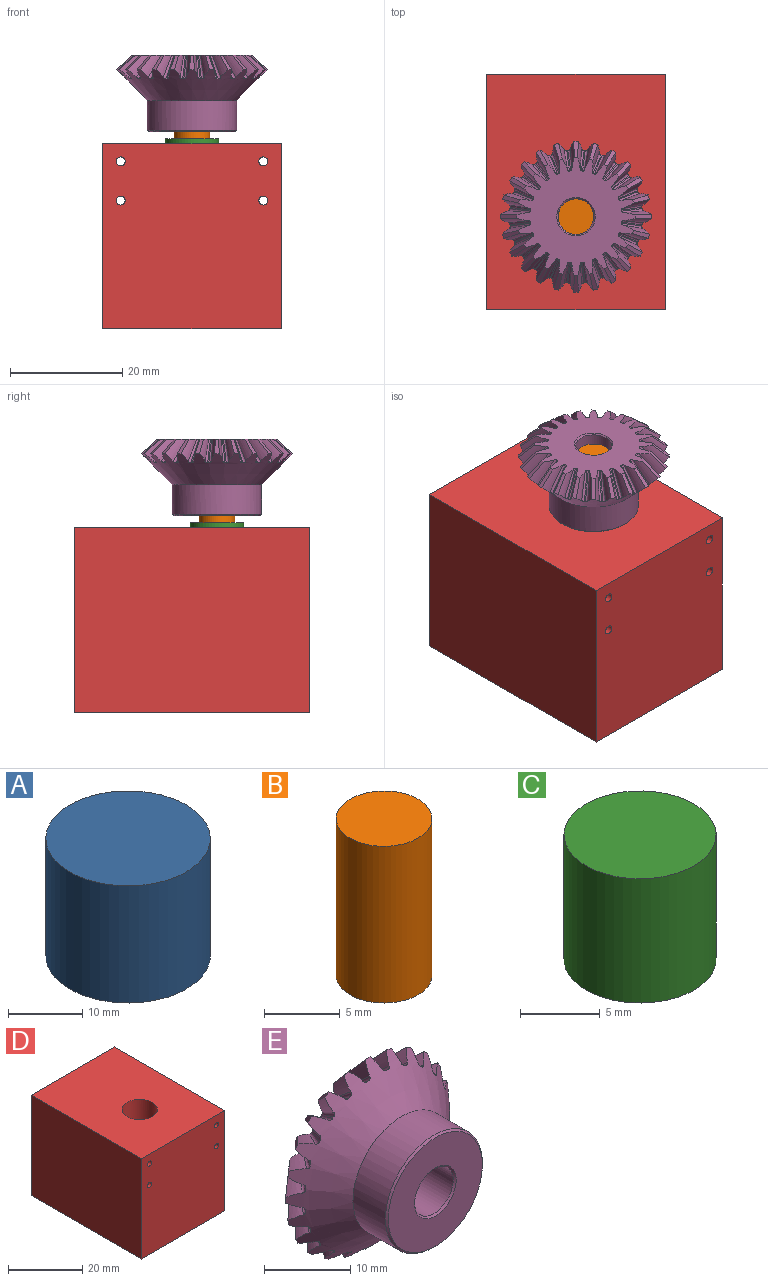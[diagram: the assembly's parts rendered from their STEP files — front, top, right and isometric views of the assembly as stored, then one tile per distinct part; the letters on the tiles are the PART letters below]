
ASSEMBLY  parts=5 mates=4
PART A: 3 faces, bbox 22.2x22.2x19.4 mm
  f0: cylinder r=11.11mm len=22.23mm, axis (0,0,-1), area 1353.2mm2, adj f1,f2
  f1: plane 22.23x22.23mm, normal (0,0,1), area 387.9mm2, adj f0
  f2: plane 22.23x22.23mm, normal (0,0,-1), area 387.9mm2, adj f0
PART B: 3 faces, bbox 6.4x6.4x12.7 mm
  f0: cylinder r=3.17mm len=12.7mm, axis (0,0,-1), area 253.4mm2, adj f1,f2
  f1: plane 6.35x6.35mm, normal (0,0,1), area 31.7mm2, adj f0
  f2: plane 6.35x6.35mm, normal (0,0,-1), area 31.7mm2, adj f0
PART C: 3 faces, bbox 9.5x9.5x9.5 mm
  f0: cylinder r=4.76mm len=9.53mm, axis (0,0,-1), area 285mm2, adj f1,f2
  f1: plane 9.53x9.53mm, normal (0,0,1), area 71.3mm2, adj f0
  f2: plane 9.53x9.53mm, normal (0,0,-1), area 71.3mm2, adj f0
PART D: 13 faces, bbox 31.8x41.9x33 mm
  f0: plane 41.91x33.02mm, normal (-1,0,0), area 1383.9mm2, adj f2,f4,f5,f12
  f1: plane 41.91x33.02mm, normal (1,0,0), area 1383.9mm2, adj f2,f4,f5,f12
  f2: plane 41.91x31.75mm, normal (0,0,-1), area 823.9mm2, adj f0,f1,f4,f6,f12
  f3: cone r=0mm half-angle=59deg, axis (0,0,-1), area 508mm2, adj f6,f7
  f4: plane 33.02x31.75mm, normal (0,1,0), area 1040.5mm2, adj f0,f1,f2,f5,f8,f9,f10,f11
  f5: plane 41.91x31.75mm, normal (0,0,1), area 1259.4mm2, adj f0,f1,f4,f7,f12
  f6: cylinder r=12.7mm len=25.4mm, axis (0,0,-1), area 1560.7mm2, adj f2,f3
  f7: cylinder r=4.76mm len=9.53mm, axis (0,0,-1), area 260.1mm2, adj f3,f5
  f8: cylinder r=0.79mm len=41.91mm, axis (0,-1,0), area 209mm2, adj f4,f12
  f9: cylinder r=0.79mm len=41.91mm, axis (0,-1,0), area 209mm2, adj f4,f12
  f10: cylinder r=0.79mm len=41.91mm, axis (0,-1,0), area 209mm2, adj f4,f12
  f11: cylinder r=0.79mm len=41.91mm, axis (0,-1,0), area 209mm2, adj f4,f12
  f12: plane 33.02x31.75mm, normal (0,-1,0), area 1040.5mm2, adj f0,f1,f2,f5,f8,f9,f10,f11
PART E: 152 faces, bbox 27.2x14.8x27.2 mm
  f0: bspline ~5.1x5.06mm, area 8.2mm2, adj f1,f4,f7,f9
  f1: cylinder r=17.7mm len=2.94mm, axis (-0.75,0.66,-0.01), area 2.8mm2, adj f0,f2,f7,f9
  f2: bspline ~5.09x5.05mm, area 8.2mm2, adj f1,f3,f7,f9
  f3: bspline ~4.47x4mm, area 2.8mm2, adj f2,f7,f8,f9
  f4: bspline ~4.47x4mm, area 2.8mm2, adj f0,f7,f9,f10
  f5: cone r=3.41mm half-angle=45deg, axis (0,1,0), area 7mm2, adj f6,f9
  f6: cylinder r=3.17mm len=13.19mm, axis (0,1,0), area 263.1mm2, adj f5,f13
  f7: cone r=13.45mm half-angle=45deg, axis (0,1,0), area 429.7mm2, adj f0,f1,f2,f3,f4,f8,f10,f14
  f8: plane 4.19x3.67mm, normal (0.75,0.66,-0.1), area 1.1mm2, adj f3,f7,f9,f151
  f9: plane 21.18x21.18mm, normal (0,1,0), area 239.8mm2, adj f0,f1,f2,f3,f4,f5,f8,f10
  f10: plane 4.19x3.67mm, normal (0.75,0.66,0.1), area 1.1mm2, adj f4,f7,f9,f18
  f11: plane 15.4x15.4mm, normal (0,-1,0), area 149.6mm2, adj f12,f13
  f12: cone r=7.94mm half-angle=45deg, axis (0,1,0), area 16.5mm2, adj f11,f14
  f13: cone r=3.41mm half-angle=45deg, axis (0,-1,0), area 7mm2, adj f6,f11
  f14: cylinder r=7.94mm len=15.88mm, axis (0,-1,0), area 264.9mm2, adj f7,f12
  f15: bspline ~5.06x5.01mm, area 8.2mm2, adj f7,f9,f16,f19
  f16: cylinder r=17.7mm len=3.03mm, axis (-0.72,0.66,-0.2), area 2.8mm2, adj f7,f9,f15,f17
  f17: bspline ~5.05x4.83mm, area 8.2mm2, adj f7,f9,f16,f18
  f18: bspline ~4.47x3.89mm, area 2.8mm2, adj f7,f9,f10,f17
  f19: bspline ~4.47x3.87mm, area 2.8mm2, adj f7,f9,f15,f20
  f20: plane 4.19x3.47mm, normal (0.69,0.66,0.29), area 1.1mm2, adj f7,f9,f19,f24
  f21: bspline ~5.06x4.58mm, area 8.2mm2, adj f7,f9,f22,f25
  f22: cylinder r=17.7mm len=2.92mm, axis (-0.64,0.66,-0.38), area 2.8mm2, adj f7,f9,f21,f23
  f23: bspline ~5.05x4.25mm, area 8.2mm2, adj f7,f9,f22,f24
  f24: bspline ~4.47x3.55mm, area 2.8mm2, adj f7,f9,f20,f23
  f25: bspline ~4.47x3.48mm, area 2.8mm2, adj f7,f9,f21,f26
  f26: plane 4.19x3.04mm, normal (0.6,0.66,0.46), area 1.1mm2, adj f7,f9,f25,f30
  f27: bspline ~5.06x3.84mm, area 8.2mm2, adj f7,f9,f28,f31
  f28: cylinder r=17.7mm len=2.65mm, axis (-0.52,0.66,-0.53), area 2.8mm2, adj f7,f9,f27,f29
  f29: bspline ~5.05x3.84mm, area 8.2mm2, adj f7,f9,f28,f30
  f30: bspline ~4.47x3.12mm, area 2.8mm2, adj f7,f9,f26,f29
  f31: bspline ~4.47x3.12mm, area 2.8mm2, adj f7,f9,f27,f32
  f32: plane 4.19x3.04mm, normal (0.46,0.66,0.6), area 1.1mm2, adj f7,f9,f31,f36
  f33: bspline ~5.06x4.25mm, area 8.2mm2, adj f7,f9,f34,f37
  f34: cylinder r=17.7mm len=2.95mm, axis (-0.37,0.66,-0.65), area 2.8mm2, adj f7,f9,f33,f35
  f35: bspline ~5.05x4.58mm, area 8.2mm2, adj f7,f9,f34,f36
  f36: bspline ~4.47x3.48mm, area 2.8mm2, adj f7,f9,f32,f35
  f37: bspline ~4.47x3.55mm, area 2.8mm2, adj f7,f9,f33,f38
  f38: plane 4.19x3.47mm, normal (0.29,0.66,0.69), area 1.1mm2, adj f7,f9,f37,f42
  f39: bspline ~5.06x4.84mm, area 8.2mm2, adj f7,f9,f40,f43
  f40: cylinder r=17.7mm len=3.04mm, axis (-0.19,0.66,-0.72), area 2.8mm2, adj f7,f9,f39,f41
  f41: bspline ~5.05x5.01mm, area 8.2mm2, adj f7,f9,f40,f42
  f42: bspline ~4.47x3.87mm, area 2.8mm2, adj f7,f9,f38,f41
  f43: bspline ~4.47x3.89mm, area 2.8mm2, adj f7,f9,f39,f44
  f44: plane 4.19x3.67mm, normal (0.1,0.66,0.75), area 1.1mm2, adj f7,f9,f43,f48
  f45: bspline ~5.1x5.06mm, area 8.2mm2, adj f7,f9,f46,f49
  f46: cylinder r=17.7mm len=2.94mm, axis (0.01,0.66,-0.75), area 2.8mm2, adj f7,f9,f45,f47
  f47: bspline ~5.09x5.05mm, area 8.2mm2, adj f7,f9,f46,f48
  f48: bspline ~4.47x4mm, area 2.8mm2, adj f7,f9,f44,f47
  f49: bspline ~4.47x4mm, area 2.8mm2, adj f7,f9,f45,f50
  f50: plane 4.19x3.67mm, normal (-0.1,0.66,0.75), area 1.1mm2, adj f7,f9,f49,f54
  f51: bspline ~5.06x5.01mm, area 8.2mm2, adj f7,f9,f52,f55
  f52: cylinder r=17.7mm len=3.03mm, axis (0.2,0.66,-0.72), area 2.8mm2, adj f7,f9,f51,f53
  f53: bspline ~5.05x4.83mm, area 8.2mm2, adj f7,f9,f52,f54
  f54: bspline ~4.47x3.89mm, area 2.8mm2, adj f7,f9,f50,f53
  f55: bspline ~4.47x3.87mm, area 2.8mm2, adj f7,f9,f51,f56
  f56: plane 4.19x3.47mm, normal (-0.29,0.66,0.69), area 1.1mm2, adj f7,f9,f55,f60
  f57: bspline ~5.06x4.58mm, area 8.2mm2, adj f7,f9,f58,f61
  f58: cylinder r=17.7mm len=2.92mm, axis (0.38,0.66,-0.64), area 2.8mm2, adj f7,f9,f57,f59
  f59: bspline ~5.05x4.25mm, area 8.2mm2, adj f7,f9,f58,f60
  f60: bspline ~4.47x3.55mm, area 2.8mm2, adj f7,f9,f56,f59
  f61: bspline ~4.47x3.48mm, area 2.8mm2, adj f7,f9,f57,f62
  f62: plane 4.19x3.04mm, normal (-0.46,0.66,0.6), area 1.1mm2, adj f7,f9,f61,f66
  f63: bspline ~5.06x3.84mm, area 8.2mm2, adj f7,f9,f64,f67
  f64: cylinder r=17.7mm len=2.65mm, axis (0.53,0.66,-0.52), area 2.8mm2, adj f7,f9,f63,f65
  f65: bspline ~5.05x3.84mm, area 8.2mm2, adj f7,f9,f64,f66
  f66: bspline ~4.47x3.12mm, area 2.8mm2, adj f7,f9,f62,f65
  f67: bspline ~4.47x3.12mm, area 2.8mm2, adj f7,f9,f63,f68
  f68: plane 4.19x3.04mm, normal (-0.6,0.66,0.46), area 1.1mm2, adj f7,f9,f67,f72
  f69: bspline ~5.06x4.25mm, area 8.2mm2, adj f7,f9,f70,f73
  f70: cylinder r=17.7mm len=2.95mm, axis (0.65,0.66,-0.37), area 2.8mm2, adj f7,f9,f69,f71
  f71: bspline ~5.05x4.58mm, area 8.2mm2, adj f7,f9,f70,f72
  f72: bspline ~4.47x3.48mm, area 2.8mm2, adj f7,f9,f68,f71
  f73: bspline ~4.47x3.55mm, area 2.8mm2, adj f7,f9,f69,f74
  f74: plane 4.19x3.47mm, normal (-0.69,0.66,0.29), area 1.1mm2, adj f7,f9,f73,f78
  f75: bspline ~5.06x4.84mm, area 8.2mm2, adj f7,f9,f76,f79
  f76: cylinder r=17.7mm len=3.04mm, axis (0.72,0.66,-0.19), area 2.8mm2, adj f7,f9,f75,f77
  f77: bspline ~5.05x5.01mm, area 8.2mm2, adj f7,f9,f76,f78
  f78: bspline ~4.47x3.87mm, area 2.8mm2, adj f7,f9,f74,f77
  f79: bspline ~4.47x3.89mm, area 2.8mm2, adj f7,f9,f75,f80
  f80: plane 4.19x3.67mm, normal (-0.75,0.66,0.1), area 1.1mm2, adj f7,f9,f79,f84
  f81: bspline ~5.1x5.06mm, area 8.2mm2, adj f7,f9,f82,f85
  f82: cylinder r=17.7mm len=2.94mm, axis (0.75,0.66,0.01), area 2.8mm2, adj f7,f9,f81,f83
  f83: bspline ~5.09x5.05mm, area 8.2mm2, adj f7,f9,f82,f84
  f84: bspline ~4.47x4mm, area 2.8mm2, adj f7,f9,f80,f83
  f85: bspline ~4.47x4mm, area 2.8mm2, adj f7,f9,f81,f86
  f86: plane 4.19x3.67mm, normal (-0.75,0.66,-0.1), area 1.1mm2, adj f7,f9,f85,f90
  f87: bspline ~5.06x5.01mm, area 8.2mm2, adj f7,f9,f88,f91
  f88: cylinder r=17.7mm len=3.03mm, axis (0.72,0.66,0.2), area 2.8mm2, adj f7,f9,f87,f89
  f89: bspline ~5.05x4.83mm, area 8.2mm2, adj f7,f9,f88,f90
  f90: bspline ~4.47x3.89mm, area 2.8mm2, adj f7,f9,f86,f89
  f91: bspline ~4.47x3.87mm, area 2.8mm2, adj f7,f9,f87,f92
  f92: plane 4.19x3.47mm, normal (-0.69,0.66,-0.29), area 1.1mm2, adj f7,f9,f91,f96
  f93: bspline ~5.06x4.58mm, area 8.2mm2, adj f7,f9,f94,f97
  f94: cylinder r=17.7mm len=2.92mm, axis (0.64,0.66,0.38), area 2.8mm2, adj f7,f9,f93,f95
  f95: bspline ~5.05x4.25mm, area 8.2mm2, adj f7,f9,f94,f96
  f96: bspline ~4.47x3.55mm, area 2.8mm2, adj f7,f9,f92,f95
  f97: bspline ~4.47x3.48mm, area 2.8mm2, adj f7,f9,f93,f98
  f98: plane 4.19x3.04mm, normal (-0.6,0.66,-0.46), area 1.1mm2, adj f7,f9,f97,f102
  f99: bspline ~5.06x3.84mm, area 8.2mm2, adj f7,f9,f100,f103
  f100: cylinder r=17.7mm len=2.65mm, axis (0.52,0.66,0.53), area 2.8mm2, adj f7,f9,f99,f101
  f101: bspline ~5.05x3.84mm, area 8.2mm2, adj f7,f9,f100,f102
  f102: bspline ~4.47x3.12mm, area 2.8mm2, adj f7,f9,f98,f101
  f103: bspline ~4.47x3.12mm, area 2.8mm2, adj f7,f9,f99,f104
  f104: plane 4.19x3.04mm, normal (-0.46,0.66,-0.6), area 1.1mm2, adj f7,f9,f103,f108
  f105: bspline ~5.06x4.25mm, area 8.2mm2, adj f7,f9,f106,f109
  f106: cylinder r=17.7mm len=2.95mm, axis (0.37,0.66,0.65), area 2.8mm2, adj f7,f9,f105,f107
  f107: bspline ~5.05x4.58mm, area 8.2mm2, adj f7,f9,f106,f108
  f108: bspline ~4.47x3.48mm, area 2.8mm2, adj f7,f9,f104,f107
  f109: bspline ~4.47x3.55mm, area 2.8mm2, adj f7,f9,f105,f110
  f110: plane 4.19x3.47mm, normal (-0.29,0.66,-0.69), area 1.1mm2, adj f7,f9,f109,f114
  f111: bspline ~5.06x4.84mm, area 8.2mm2, adj f7,f9,f112,f115
  f112: cylinder r=17.7mm len=3.04mm, axis (0.19,0.66,0.72), area 2.8mm2, adj f7,f9,f111,f113
  f113: bspline ~5.05x5.01mm, area 8.2mm2, adj f7,f9,f112,f114
  f114: bspline ~4.47x3.87mm, area 2.8mm2, adj f7,f9,f110,f113
  f115: bspline ~4.47x3.89mm, area 2.8mm2, adj f7,f9,f111,f116
  f116: plane 4.19x3.67mm, normal (-0.1,0.66,-0.75), area 1.1mm2, adj f7,f9,f115,f120
  f117: bspline ~5.1x5.06mm, area 8.2mm2, adj f7,f9,f118,f121
  f118: cylinder r=17.7mm len=2.94mm, axis (-0.01,0.66,0.75), area 2.8mm2, adj f7,f9,f117,f119
  f119: bspline ~5.09x5.05mm, area 8.2mm2, adj f7,f9,f118,f120
  f120: bspline ~4.47x4mm, area 2.8mm2, adj f7,f9,f116,f119
  f121: bspline ~4.47x4mm, area 2.8mm2, adj f7,f9,f117,f122
  f122: plane 4.19x3.67mm, normal (0.1,0.66,-0.75), area 1.1mm2, adj f7,f9,f121,f126
  f123: bspline ~5.06x5.01mm, area 8.2mm2, adj f7,f9,f124,f127
  f124: cylinder r=17.7mm len=3.03mm, axis (-0.2,0.66,0.72), area 2.8mm2, adj f7,f9,f123,f125
  f125: bspline ~5.05x4.83mm, area 8.2mm2, adj f7,f9,f124,f126
  f126: bspline ~4.47x3.89mm, area 2.8mm2, adj f7,f9,f122,f125
  f127: bspline ~4.47x3.87mm, area 2.8mm2, adj f7,f9,f123,f128
  f128: plane 4.19x3.47mm, normal (0.29,0.66,-0.69), area 1.1mm2, adj f7,f9,f127,f132
  f129: bspline ~5.06x4.58mm, area 8.2mm2, adj f7,f9,f130,f133
  f130: cylinder r=17.7mm len=2.92mm, axis (-0.38,0.66,0.64), area 2.8mm2, adj f7,f9,f129,f131
  f131: bspline ~5.05x4.25mm, area 8.2mm2, adj f7,f9,f130,f132
  f132: bspline ~4.47x3.55mm, area 2.8mm2, adj f7,f9,f128,f131
  f133: bspline ~4.47x3.48mm, area 2.8mm2, adj f7,f9,f129,f134
  f134: plane 4.19x3.04mm, normal (0.46,0.66,-0.6), area 1.1mm2, adj f7,f9,f133,f138
  f135: bspline ~5.06x3.84mm, area 8.2mm2, adj f7,f9,f136,f139
  f136: cylinder r=17.7mm len=2.65mm, axis (-0.53,0.66,0.52), area 2.8mm2, adj f7,f9,f135,f137
  f137: bspline ~5.05x3.84mm, area 8.2mm2, adj f7,f9,f136,f138
  f138: bspline ~4.47x3.12mm, area 2.8mm2, adj f7,f9,f134,f137
  f139: bspline ~4.47x3.12mm, area 2.8mm2, adj f7,f9,f135,f140
  f140: plane 4.19x3.04mm, normal (0.6,0.66,-0.46), area 1.1mm2, adj f7,f9,f139,f144
  f141: bspline ~5.06x4.25mm, area 8.2mm2, adj f7,f9,f142,f145
  f142: cylinder r=17.7mm len=2.95mm, axis (-0.65,0.66,0.37), area 2.8mm2, adj f7,f9,f141,f143
  f143: bspline ~5.05x4.58mm, area 8.2mm2, adj f7,f9,f142,f144
  f144: bspline ~4.47x3.48mm, area 2.8mm2, adj f7,f9,f140,f143
  f145: bspline ~4.47x3.55mm, area 2.8mm2, adj f7,f9,f141,f146
  f146: plane 4.19x3.47mm, normal (0.69,0.66,-0.29), area 1.1mm2, adj f7,f9,f145,f150
  f147: bspline ~5.06x4.84mm, area 8.2mm2, adj f7,f9,f148,f151
  f148: cylinder r=17.7mm len=3.04mm, axis (-0.72,0.66,0.19), area 2.8mm2, adj f7,f9,f147,f149
  f149: bspline ~5.05x5.01mm, area 8.2mm2, adj f7,f9,f148,f150
  f150: bspline ~4.47x3.87mm, area 2.8mm2, adj f7,f9,f146,f149
  f151: bspline ~4.47x3.89mm, area 2.8mm2, adj f7,f8,f9,f147
PLACE A t=(-8,-0.15,-2.99)mm fixed
PLACE B t=(-8,-0.15,25.91)mm
PLACE C t=(-8,-0.15,16.39)mm
PLACE D t=(-8,-0.15,-7.94)mm
PLACE E rot(axis=(1,0,0),90deg) t=(-8,-0.15,37.49)mm
MATE fastened C.f0 <-> B.f0  axis (0,0,1) through (-8,-0.15,25.91)mm
MATE fastened D.f3 <-> C.f0  axis (0,0,-1) through (-8,-0.15,16.39)mm
MATE fastened A.f0 <-> C.f0  axis (0,0,1) through (-8,-0.15,16.39)mm
MATE fastened B.f0 <-> E.f5  axis (0,0,-1) through (-8,-0.15,27.18)mm
